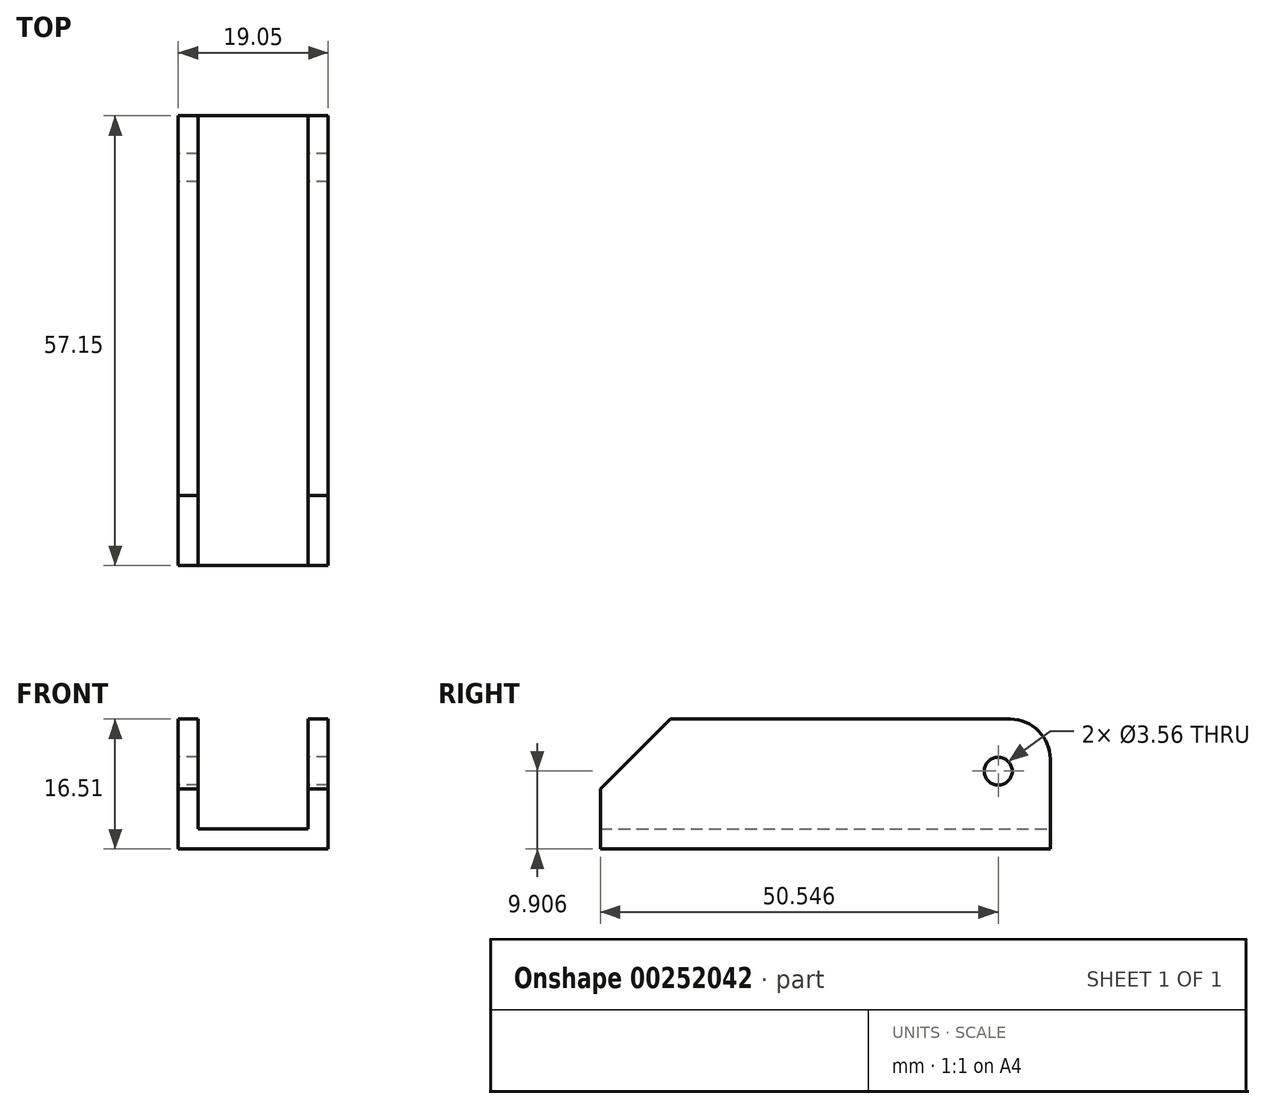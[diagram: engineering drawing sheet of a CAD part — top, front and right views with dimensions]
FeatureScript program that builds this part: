
annotation { "Feature Type Name" : "Feature", "Feature Type Description" : "" }
export const myFeature = defineFeature(function(context is Context, id is Id, definition is map)
    precondition{}
    {
        {
            var Q0;
            Q0=qCreatedBy(makeId("Front.planeOp"),FACE);
            var sketch = newSketch(context, id + "F0", { "sketchPlane" : qUnion([Q0])});
            skLineSegment(sketch, "E0.bottom", {"start": v(0, 0) * mm, "end": v(19.05, 0) * mm});
            skLineSegment(sketch, "E0.top", {"start": v(0, 16.51) * mm, "end": v(2.54, 16.51) * mm});
            skLineSegment(sketch, "E0.left", {"start": v(0, 0) * mm, "end": v(0, 16.51) * mm});
            skLineSegment(sketch, "E0.right", {"start": v(19.05, 0) * mm, "end": v(19.05, 16.51) * mm});
            skLineSegment(sketch, "E1", {"start": v(9.52, 0) * mm, "end": v(9.52, 16.51) * mm, "construction": true});
            skLineSegment(sketch, "E2", {"start": v(2.54, 16.51) * mm, "end": v(2.54, 2.54) * mm});
            skLineSegment(sketch, "E3", {"start": v(2.54, 2.54) * mm, "end": v(16.51, 2.54) * mm});
            skLineSegment(sketch, "E4", {"start": v(16.51, 2.54) * mm, "end": v(16.51, 16.51) * mm});
            skLineSegment(sketch, "E5.trimOffspring", {"start": v(16.51, 16.51) * mm, "end": v(19.05, 16.51) * mm});
            skSolve(sketch);
        }
        {
            var Q0;
            Q0 = qSketchRegion(id + "F0", true);
            extrude(context, id + "F1", {"entities" : qUnion([Q0]), "depth" : 57.15 * mm});
        }
        {
            var Q0;
            Q0=makeQuery(id+"F1.opExtrude","SWEPT_FACE",FACE,{"disambiguationData":[OSD([sQuery(id+"F0.wireOp",EDGE,"E0.left")])]});
            var sketch = newSketch(context, id + "F2", { "sketchPlane" : qUnion([Q0])});
            skLineSegment(sketch, "E6", {"start": v(0, 9.9) * mm, "end": v(6.6, 9.9) * mm, "construction": true});
            skCircle(sketch, "E7", {"center": v(6.6, 9.9) * mm, "radius": 1.78 * mm});
            skSolve(sketch);
        }
        {
            var Q0;
            Q0 = qSketchRegion(id + "F2", true);
            extrude(context, id + "F3", {"entities" : qUnion([Q0]), "operationType" : NewBodyOperationType.REMOVE, "endBound" : BoundingType.THROUGH_ALL, "oppositeDirection" : true, "depth" : 25.4 * mm});
        }
        {
            var Q0;
            Q0=makeQuery(id+"F1.opExtrude","CAP_EDGE",EDGE,{"disambiguationData":[OSD([sQuery(id+"F0.wireOp",EDGE,"E5.trimOffspring")])],"isStart":true});
            var Q1;
            Q1=makeQuery(id+"F1.opExtrude","CAP_EDGE",EDGE,{"disambiguationData":[OSD([sQuery(id+"F0.wireOp",EDGE,"E0.top")])],"isStart":true});
            fillet(context, id + "F4", {"entities" : qUnion([Q0, Q1]), "radius" : 5.08 * mm, "tangentPropagation" : true, "allowEdgeOverflow" : false});
        }
        {
            var Q0;
            Q0=makeQuery(id+"F1.opExtrude","CAP_EDGE",EDGE,{"disambiguationData":[OSD([sQuery(id+"F0.wireOp",EDGE,"E0.top")])],"isStart":false});
            var Q1;
            Q1=makeQuery(id+"F1.opExtrude","CAP_EDGE",EDGE,{"disambiguationData":[OSD([sQuery(id+"F0.wireOp",EDGE,"E5.trimOffspring")])],"isStart":false});
            chamfer(context, id + "F5", {"entities" : qUnion([Q0, Q1]), "width" : 8.9 * mm, "tangentPropagation" : true});
        }
    });
